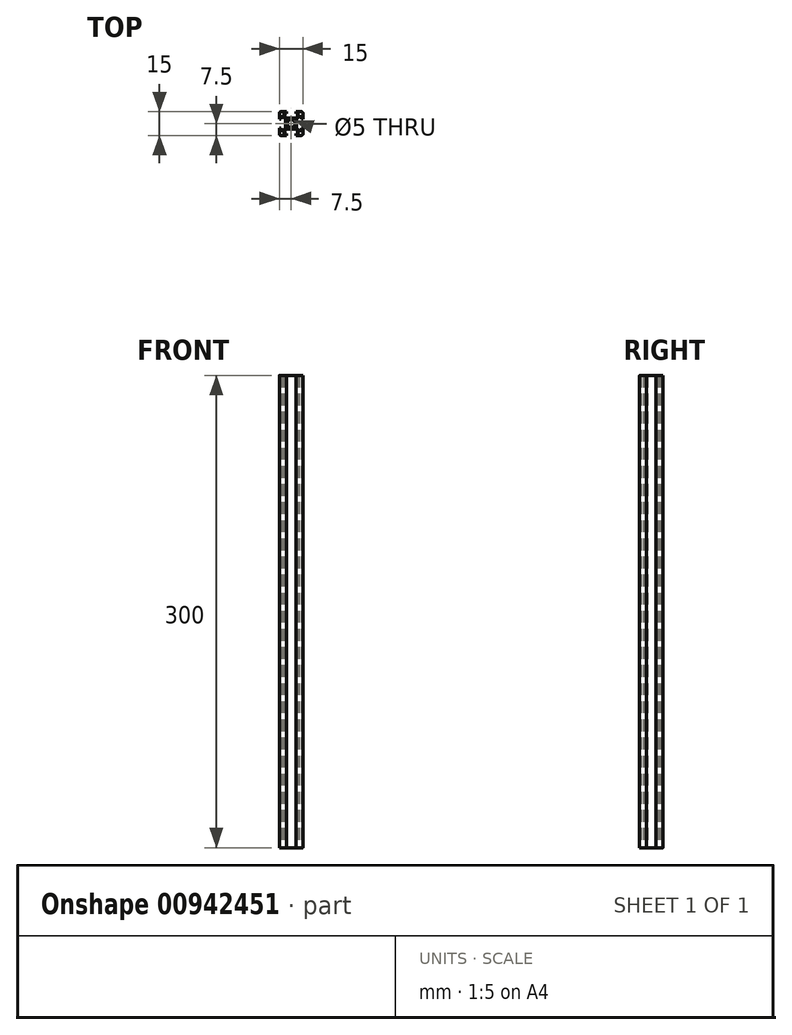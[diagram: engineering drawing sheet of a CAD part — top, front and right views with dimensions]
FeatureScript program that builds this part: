
annotation { "Feature Type Name" : "Feature", "Feature Type Description" : "" }
export const myFeature = defineFeature(function(context is Context, id is Id, definition is map)
    precondition{}
    {
        {
            assignVariable(context, id + "F0", {"name" : "height", "anyValue" : 300});
        }
        {
            var Q0;
            Q0=qCreatedBy(makeId("Top.planeOp"),FACE);
            var sketch = newSketch(context, id + "F1", { "sketchPlane" : qUnion([Q0])});
            skCircle(sketch, "E0", {"center": v(0, 0) * mm, "radius": 2.5 * mm});
            skLineSegment(sketch, "E1.bottom", {"start": v(6.5, 7.5) * mm, "end": v(3, 7.5) * mm});
            skLineSegment(sketch, "E1.top", {"start": v(6.5, -7.5) * mm, "end": v(3, -7.5) * mm});
            skLineSegment(sketch, "E1.left", {"start": v(7.5, 6.5) * mm, "end": v(7.5, 3) * mm});
            skLineSegment(sketch, "E1.right", {"start": v(-7.5, 6.5) * mm, "end": v(-7.5, 3) * mm});
            skPoint(sketch, "E2.visualSharp", {"position": v(-7.5, 7.5) * mm});
            skArc(sketch, "E2.filletArc", {"start": v(-6.5, 7.5) * mm, "mid": v(-7.2, 7.2) * mm, "end": v(-7.5, 6.5) * mm});
            skPoint(sketch, "E3.visualSharp", {"position": v(7.5, 7.5) * mm});
            skArc(sketch, "E3.filletArc", {"start": v(7.5, 6.5) * mm, "mid": v(7.2, 7.2) * mm, "end": v(6.5, 7.5) * mm});
            skPoint(sketch, "E4.visualSharp", {"position": v(7.5, -7.5) * mm});
            skArc(sketch, "E4.filletArc", {"start": v(6.5, -7.5) * mm, "mid": v(7.2, -7.2) * mm, "end": v(7.5, -6.5) * mm});
            skPoint(sketch, "E5.visualSharp", {"position": v(-7.5, -7.5) * mm});
            skArc(sketch, "E5.filletArc", {"start": v(-7.5, -6.5) * mm, "mid": v(-7.2, -7.2) * mm, "end": v(-6.5, -7.5) * mm});
            skLineSegment(sketch, "E6", {"start": v(-3, 7.5) * mm, "end": v(-3, 6.5) * mm});
            skLineSegment(sketch, "E7", {"start": v(3, 7.5) * mm, "end": v(3, 6.5) * mm});
            skLineSegment(sketch, "E8", {"start": v(-4.5, 6.5) * mm, "end": v(-4.5, 5) * mm});
            skLineSegment(sketch, "E9", {"start": v(4.5, 5) * mm, "end": v(4.5, 6.5) * mm});
            skLineSegment(sketch, "E10", {"start": v(4.5, 6.5) * mm, "end": v(3, 6.5) * mm});
            skLineSegment(sketch, "E11", {"start": v(-3, 3.5) * mm, "end": v(3, 3.5) * mm});
            skLineSegment(sketch, "E12", {"start": v(3, 3.5) * mm, "end": v(4.5, 5) * mm});
            skLineSegment(sketch, "E13", {"start": v(-3, 3.5) * mm, "end": v(-4.5, 5) * mm});
            skLineSegment(sketch, "E14.trimOffspring", {"start": v(-3, 6.5) * mm, "end": v(-4.5, 6.5) * mm});
            skLineSegment(sketch, "E15", {"start": v(-3, -7.5) * mm, "end": v(-3, -6.5) * mm});
            skLineSegment(sketch, "E16", {"start": v(-3, -6.5) * mm, "end": v(-4.5, -6.5) * mm});
            skLineSegment(sketch, "E17", {"start": v(-4.5, -6.5) * mm, "end": v(-4.5, -5) * mm});
            skLineSegment(sketch, "E18", {"start": v(-4.5, -5) * mm, "end": v(-3, -3.5) * mm});
            skLineSegment(sketch, "E19", {"start": v(-3, -3.5) * mm, "end": v(3, -3.5) * mm});
            skLineSegment(sketch, "E20", {"start": v(3, -3.5) * mm, "end": v(4.5, -5) * mm});
            skLineSegment(sketch, "E21", {"start": v(4.5, -5) * mm, "end": v(4.5, -6.5) * mm});
            skLineSegment(sketch, "E22", {"start": v(4.5, -6.5) * mm, "end": v(3, -6.5) * mm});
            skLineSegment(sketch, "E23", {"start": v(3, -6.5) * mm, "end": v(3, -7.5) * mm});
            skPoint(sketch, "E24", {"position": v(0, 7.5) * mm});
            skPoint(sketch, "E25", {"position": v(0, -7.5) * mm});
            skPoint(sketch, "E26", {"position": v(7.5, 0) * mm});
            skPoint(sketch, "E27", {"position": v(-7.5, 0) * mm});
            skLineSegment(sketch, "E28", {"start": v(7.5, 3) * mm, "end": v(6.5, 3) * mm});
            skLineSegment(sketch, "E29", {"start": v(6.5, 3) * mm, "end": v(6.5, 4.5) * mm});
            skLineSegment(sketch, "E30", {"start": v(6.5, 4.5) * mm, "end": v(5, 4.5) * mm});
            skLineSegment(sketch, "E31", {"start": v(5, 4.5) * mm, "end": v(3.5, 3) * mm});
            skLineSegment(sketch, "E32", {"start": v(3.5, 3) * mm, "end": v(3.5, -3) * mm});
            skLineSegment(sketch, "E33", {"start": v(3.5, -3) * mm, "end": v(5, -4.5) * mm});
            skLineSegment(sketch, "E34", {"start": v(5, -4.5) * mm, "end": v(6.5, -4.5) * mm});
            skLineSegment(sketch, "E35", {"start": v(6.5, -4.5) * mm, "end": v(6.5, -3) * mm});
            skLineSegment(sketch, "E36", {"start": v(6.5, -3) * mm, "end": v(7.5, -3) * mm});
            skLineSegment(sketch, "E37.trimOffspring", {"start": v(-3, 7.5) * mm, "end": v(-6.5, 7.5) * mm});
            skLineSegment(sketch, "E38.trimOffspring", {"start": v(7.5, -3) * mm, "end": v(7.5, -6.5) * mm});
            skLineSegment(sketch, "E39.trimOffspring", {"start": v(-3, -7.5) * mm, "end": v(-6.5, -7.5) * mm});
            skLineSegment(sketch, "E40", {"start": v(-7.5, 3) * mm, "end": v(-6.5, 3) * mm});
            skLineSegment(sketch, "E41", {"start": v(-6.5, 3) * mm, "end": v(-6.5, 4.5) * mm});
            skLineSegment(sketch, "E42", {"start": v(-6.5, 4.5) * mm, "end": v(-5, 4.5) * mm});
            skLineSegment(sketch, "E43", {"start": v(-5, 4.5) * mm, "end": v(-3.5, 3) * mm});
            skLineSegment(sketch, "E44", {"start": v(-3.5, 3) * mm, "end": v(-3.5, -3) * mm});
            skLineSegment(sketch, "E45", {"start": v(-3.5, -3) * mm, "end": v(-5, -4.5) * mm});
            skLineSegment(sketch, "E46", {"start": v(-5, -4.5) * mm, "end": v(-6.5, -4.5) * mm});
            skLineSegment(sketch, "E47", {"start": v(-6.5, -4.5) * mm, "end": v(-6.5, -3) * mm});
            skLineSegment(sketch, "E48", {"start": v(-6.5, -3) * mm, "end": v(-7.5, -3) * mm});
            skLineSegment(sketch, "E49.trimOffspring", {"start": v(-7.5, -3) * mm, "end": v(-7.5, -6.5) * mm});
            skSolve(sketch);
        }
        {
            var Q0;
            Q0=qSketchRegion(id+"F1",true);
            extrude(context, id + "F2", {"entities" : qUnion([Q0]), "depth" : (getVariable(context, 'height')) * mm, "offsetDistance" : 25 * mm});
        }
    });
